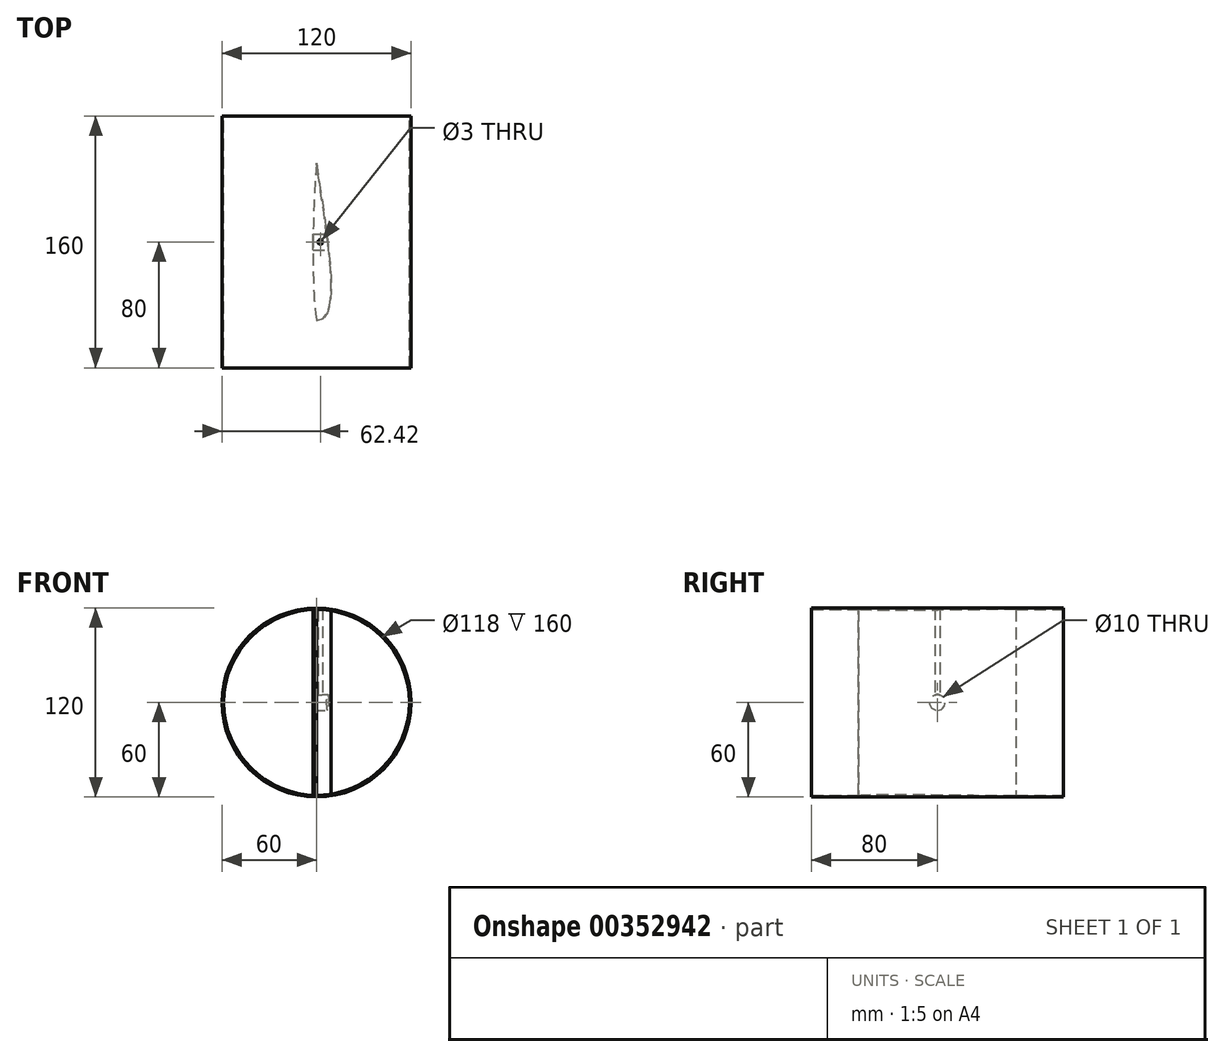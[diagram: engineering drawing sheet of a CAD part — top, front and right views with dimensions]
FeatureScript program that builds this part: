
annotation { "Feature Type Name" : "Feature", "Feature Type Description" : "" }
export const myFeature = defineFeature(function(context is Context, id is Id, definition is map)
    precondition{}
    {
        {
            var Q0;
            Q0=qCreatedBy(makeId("Front.planeOp"),FACE);
            var sketch = newSketch(context, id + "F0", { "sketchPlane" : qUnion([Q0])});
            skCircle(sketch, "E0", {"center": v(0, 0) * mm, "radius": 60 * mm});
            skCircle(sketch, "E1", {"center": v(0, 0) * mm, "radius": 59 * mm});
            skSolve(sketch);
        }
        {
            var Q0;
            Q0 = qSketchRegion(id + "F0", true);
            extrude(context, id + "F1", {"entities" : qUnion([Q0]), "depth" : 80 * mm, "hasSecondDirection" : true, "secondDirectionOppositeDirection" : true, "secondDirectionDepth" : 80 * mm});
        }
        {
            var Q0;
            Q0=qCreatedBy(makeId("Top.planeOp"),FACE);
            var sketch = newSketch(context, id + "F2", { "sketchPlane" : qUnion([Q0])});
            skLineSegment(sketch, "E2", {"start": v(0, -50) * mm, "end": v(0, 50) * mm, "construction": true});
            skFitSpline(sketch, "E3", {"points": [v(0, -50) * mm, v(0, 50) * mm], "startDerivative": vector(49.53, -0.46) * mm, "endDerivative": vector(-21.67, 150) * mm});
            skFitSpline(sketch, "E4", {"points": [v(0, -50) * mm, v(0, 50) * mm], "startDerivative": vector(-9.9, 54.65) * mm, "endDerivative": vector(8.05, 94.28) * mm});
            skCircle(sketch, "E5", {"center": v(2.42, 0) * mm, "radius": 1.5 * mm});
            skSolve(sketch);
        }
        {
            var Q0;
            Q0=makeQuery(id+"F2.imprint","IMPRINT",FACE,{"disambiguationData":[TD([[makeQuery(id+"F2.imprint","IMPRINT",EDGE,{"derivedFrom":sQuery(id+"F2.wireOp",EDGE,"E3")}),1.0]])]});
            var Q1;
            Q1=makeQuery(id+"F2.imprint","IMPRINT",FACE,{"disambiguationData":[TD([[makeQuery(id+"F2.imprint","IMPRINT",EDGE,{"derivedFrom":sQuery(id+"F2.wireOp",EDGE,"E5")}),1.0]])]});
            extrude(context, id + "F3", {"entities" : qUnion([Q0, Q1]), "operationType" : NewBodyOperationType.ADD, "endBound" : BoundingType.UP_TO_NEXT, "depth" : 25 * mm, "hasSecondDirection" : true, "secondDirectionBound" : SecondDirectionBoundingType.UP_TO_NEXT, "secondDirectionOppositeDirection" : true, "secondDirectionDepth" : 25 * mm});
        }
        {
            var Q0;
            Q0=qCreatedBy(makeId("Right.planeOp"),FACE);
            var sketch = newSketch(context, id + "F4", { "sketchPlane" : qUnion([Q0])});
            skCircle(sketch, "E6", {"center": v(0, 0) * mm, "radius": 5 * mm});
            skSolve(sketch);
        }
        {
            var Q0;
            Q0 = qSketchRegion(id + "F4", true);
            var Q1;
            Q1=makeQuery(id+"F3.opExtrude","SWEPT_FACE",FACE,{"disambiguationData":[OSD([sQuery(id+"F2.wireOp",EDGE,"E3")])]});
            var Q2;
            Q2=makeQuery(id+"F3.opExtrude","SWEPT_FACE",FACE,{"disambiguationData":[OSD([sQuery(id+"F2.wireOp",EDGE,"E4")])]});
            extrude(context, id + "F5", {"entities" : qUnion([Q0]), "operationType" : NewBodyOperationType.REMOVE, "endBound" : BoundingType.UP_TO_NEXT, "oppositeDirection" : true, "endBoundEntityFace" : qUnion([Q1]), "depth" : 25 * mm, "hasSecondDirection" : true, "secondDirectionBound" : SecondDirectionBoundingType.UP_TO_NEXT, "secondDirectionOppositeDirection" : false, "secondDirectionBoundEntityFace" : qUnion([Q2]), "secondDirectionDepth" : 25 * mm});
        }
        {
            var Q0;
            Q0=makeQuery(id+"F2.imprint","IMPRINT",FACE,{"disambiguationData":[TD([[makeQuery(id+"F2.imprint","IMPRINT",EDGE,{"derivedFrom":sQuery(id+"F2.wireOp",EDGE,"E5")}),1.0]])]});
            extrude(context, id + "F6", {"entities" : qUnion([Q0]), "operationType" : NewBodyOperationType.REMOVE, "endBound" : BoundingType.THROUGH_ALL, "depth" : 25 * mm});
        }
    });
